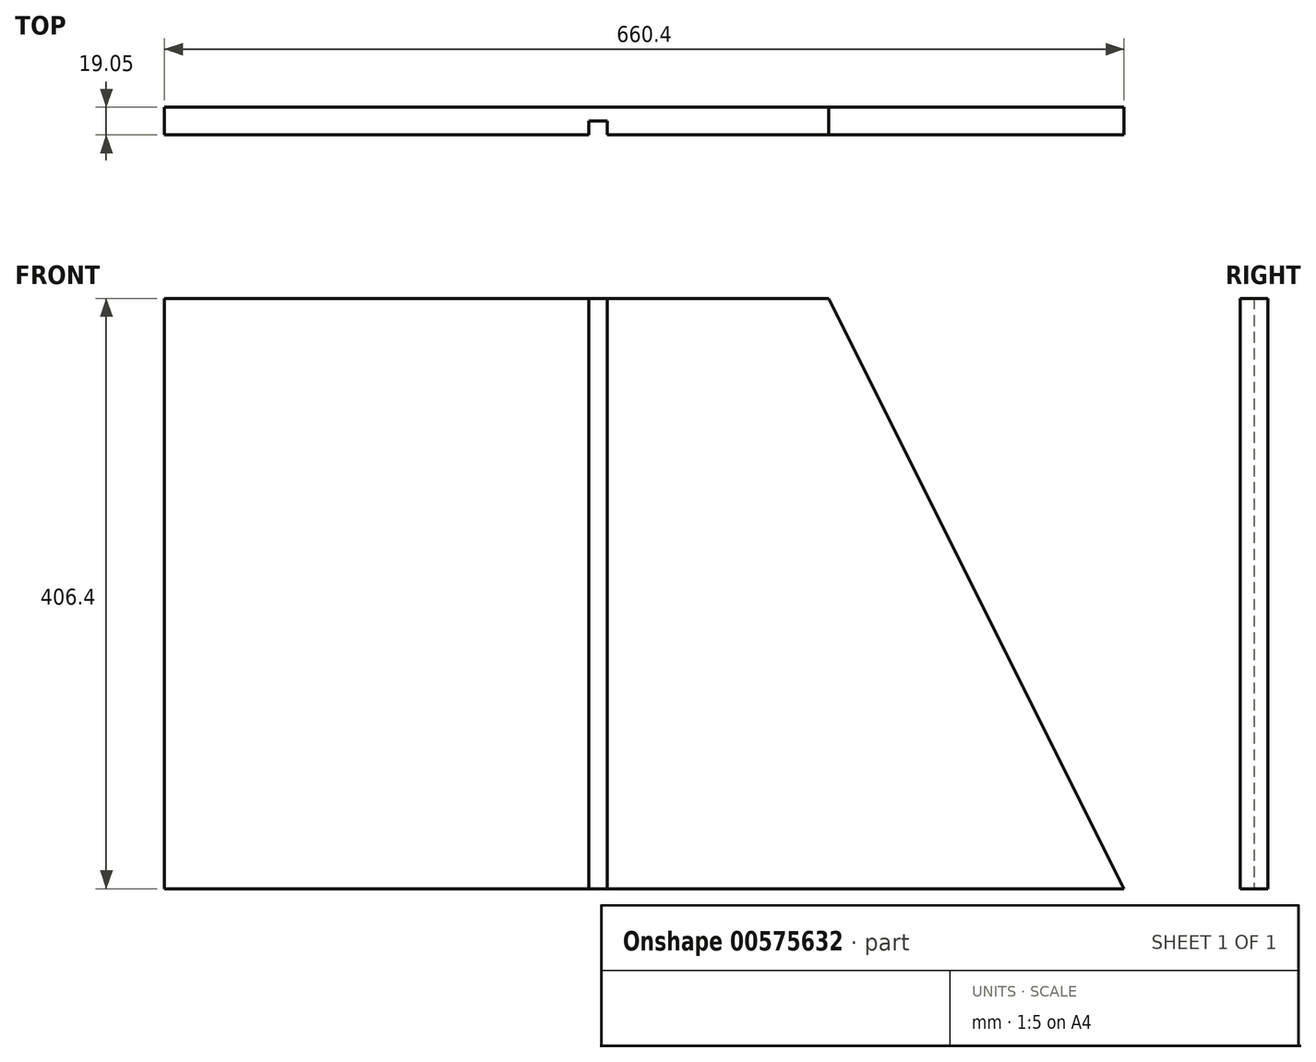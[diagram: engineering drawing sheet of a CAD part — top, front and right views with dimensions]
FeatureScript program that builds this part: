
annotation { "Feature Type Name" : "Feature", "Feature Type Description" : "" }
export const myFeature = defineFeature(function(context is Context, id is Id, definition is map)
    precondition{}
    {
        {
            var Q0;
            Q0=qCreatedBy(makeId("Front.planeOp"),FACE);
            var sketch = newSketch(context, id + "F0", { "sketchPlane" : qUnion([Q0])});
            skLineSegment(sketch, "E0", {"start": v(-356.65, 252.41) * mm, "end": v(-229.65, 252.41) * mm});
            skLineSegment(sketch, "E1", {"start": v(-229.65, 252.41) * mm, "end": v(-26.45, -153.99) * mm});
            skLineSegment(sketch, "E2", {"start": v(-26.45, -153.99) * mm, "end": v(-686.85, -153.99) * mm});
            skLineSegment(sketch, "E3", {"start": v(-229.65, 252.41) * mm, "end": v(-229.65, -153.99) * mm});
            skLineSegment(sketch, "E4.bottom", {"start": v(-356.65, 252.41) * mm, "end": v(-686.85, 252.41) * mm});
            skLineSegment(sketch, "E4.top", {"start": v(-356.65, -153.99) * mm, "end": v(-686.85, -153.99) * mm});
            skLineSegment(sketch, "E4.right", {"start": v(-686.85, 252.41) * mm, "end": v(-686.85, -153.99) * mm});
            skSolve(sketch);
        }
        {
            var Q0;
            {var subQ0=sQuery(id+"F0.wireOp",EDGE,"nFMApCBA-aBbS-xDlN-ZNX0-Un9WT2dHDHLE");Q0=makeQuery(id+"F0.imprint","IMPRINT",FACE,{"disambiguationData":[TD([[makeQuery(id+"F0.imprint","IMPRINT",EDGE,{"derivedFrom":subQ0}),-1.0]])]});}
            var Q1;
            Q1=makeQuery(id+"F0.imprint","IMPRINT",FACE,{"disambiguationData":[TD([[makeQuery(id+"F0.imprint","IMPRINT",EDGE,{"derivedFrom":sQuery(id+"F0.wireOp",EDGE,"E0")}),-1.0]])]});
            var Q2;
            {var subQ0=sQuery(id+"F0.wireOp",EDGE,"E1");Q2=makeQuery(id+"F0.imprint","IMPRINT",FACE,{"disambiguationData":[TD([[makeQuery(id+"F0.imprint","IMPRINT",EDGE,{"derivedFrom":subQ0}),-1.0]])]});}
            extrude(context, id + "F1", {"entities" : qUnion([Q0, Q1, Q2]), "depth" : 19.05 * mm, "offsetDistance" : 25.4 * mm});
        }
        {
            var Q0;
            Q0=makeQuery(id+"F1.opExtrude","CAP_FACE",FACE,{"disambiguationData":[OSD([sQuery(id+"F0.wireOp",EDGE,"E0"),sQuery(id+"F0.wireOp",EDGE,"E1"),sQuery(id+"F0.wireOp",EDGE,"E2"),sQuery(id+"F0.wireOp",EDGE,"nFMApCBA-aBbS-xDlN-ZNX0-Un9WT2dHDHLE")])],"isStart":false});
            var sketch = newSketch(context, id + "F2", { "sketchPlane" : qUnion([Q0])});
            skLineSegment(sketch, "E5", {"start": v(-229.65, 252.41) * mm, "end": v(-229.65, -153.99) * mm});
            skLineSegment(sketch, "E6.0", {"start": v(-382.05, 252.41) * mm, "end": v(-382.05, -153.99) * mm});
            skLineSegment(sketch, "E7.0", {"start": v(-394.75, 252.41) * mm, "end": v(-394.75, -153.99) * mm});
            skLineSegment(sketch, "E8.bottom", {"start": v(-394.75, 252.41) * mm, "end": v(-382.05, 252.41) * mm});
            skLineSegment(sketch, "E8.top", {"start": v(-394.75, -153.99) * mm, "end": v(-382.05, -153.99) * mm});
            skSolve(sketch);
        }
        {
            var Q0;
            Q0=qSketchRegion(id+"F2",true);
            extrude(context, id + "F3", {"entities" : qUnion([Q0]), "operationType" : NewBodyOperationType.REMOVE, "oppositeDirection" : true, "depth" : 9.52 * mm, "offsetDistance" : 25.4 * mm});
        }
    });
